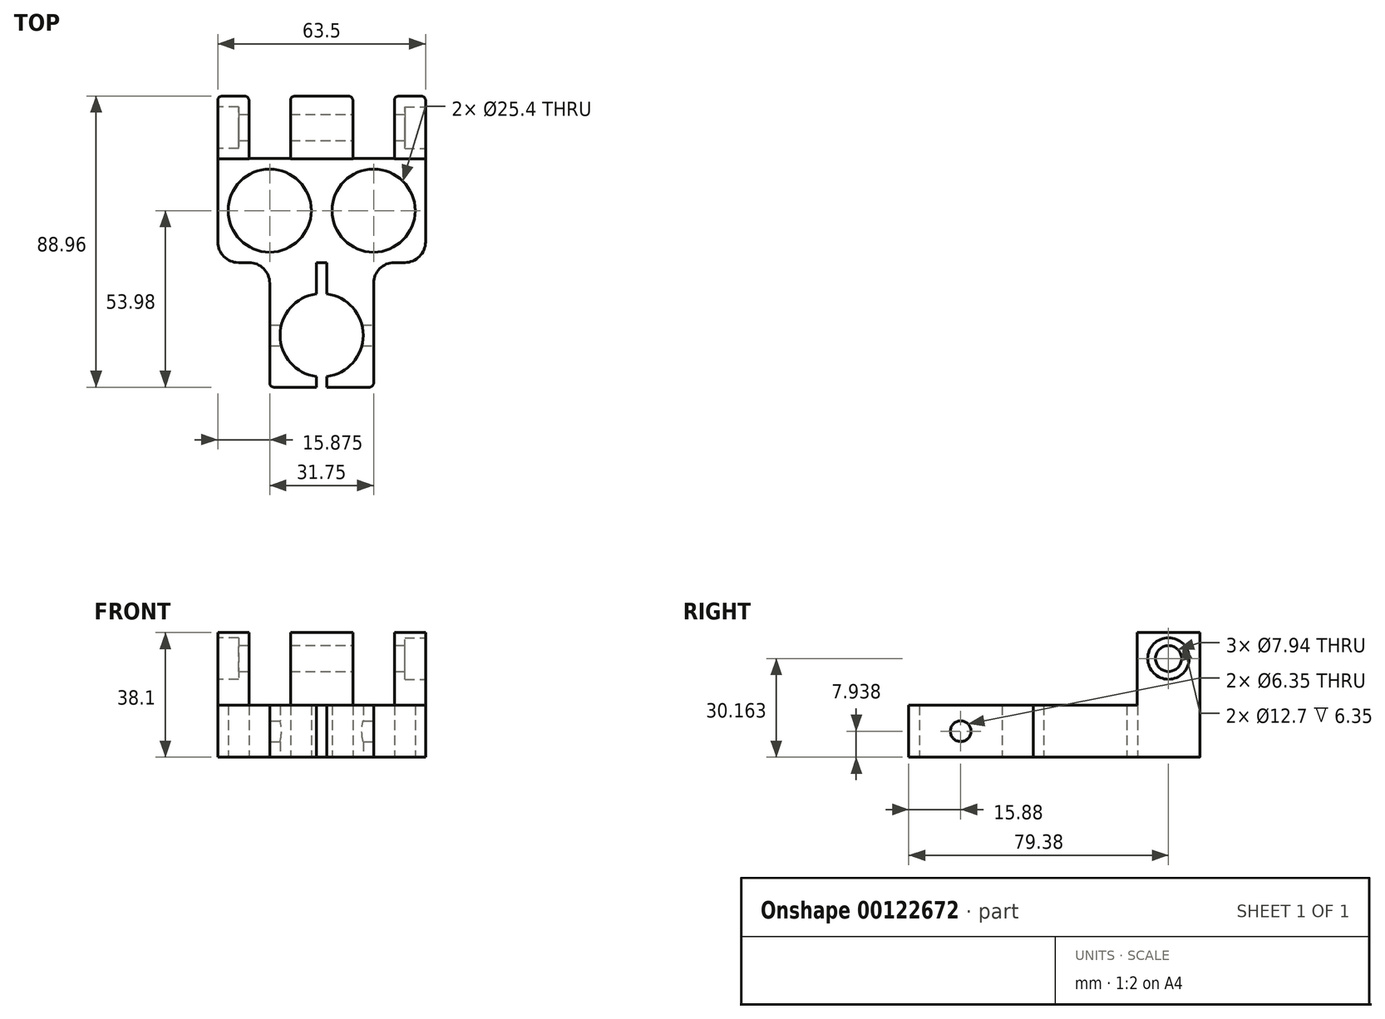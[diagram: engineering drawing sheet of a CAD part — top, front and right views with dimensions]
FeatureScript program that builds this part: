
annotation { "Feature Type Name" : "Feature", "Feature Type Description" : "" }
export const myFeature = defineFeature(function(context is Context, id is Id, definition is map)
    precondition{}
    {
        {
            var Q0;
            Q0=qCreatedBy(makeId("Top.planeOp"),FACE);
            var sketch = newSketch(context, id + "F0", { "sketchPlane" : qUnion([Q0])});
            skCircle(sketch, "E0", {"center": v(-15.88, 0) * mm, "radius": 12.7 * mm});
            skCircle(sketch, "E1", {"center": v(15.88, 0) * mm, "radius": 12.7 * mm});
            skArc(sketch, "E2", {"start": v(-1.59, -25.5) * mm, "mid": v(-12.7, -38.1) * mm, "end": v(-1.59, -50.7) * mm});
            skLineSegment(sketch, "E3", {"start": v(-14.6, -53.98) * mm, "end": v(-1.59, -53.98) * mm});
            skLineSegment(sketch, "E4", {"start": v(15.88, -52.7) * mm, "end": v(15.87, -22.23) * mm});
            skLineSegment(sketch, "E5", {"start": v(22.23, -15.88) * mm, "end": v(25.4, -15.88) * mm});
            skLineSegment(sketch, "E6", {"start": v(31.75, -9.53) * mm, "end": v(31.75, 33.7) * mm});
            skLineSegment(sketch, "E7", {"start": v(30.48, 34.98) * mm, "end": v(23.5, 34.98) * mm});
            skLineSegment(sketch, "E8", {"start": v(22.22, 33.7) * mm, "end": v(22.22, 15.99) * mm});
            skLineSegment(sketch, "E9", {"start": v(22.16, 15.93) * mm, "end": v(9.59, 15.93) * mm});
            skLineSegment(sketch, "E10", {"start": v(9.53, 15.99) * mm, "end": v(9.53, 33.7) * mm});
            skLineSegment(sketch, "E11", {"start": v(8.26, 34.98) * mm, "end": v(-8.26, 34.98) * mm});
            skLineSegment(sketch, "E12", {"start": v(-23.5, 34.98) * mm, "end": v(-30.48, 34.98) * mm});
            skLineSegment(sketch, "E13", {"start": v(-31.75, 33.7) * mm, "end": v(-31.75, -9.53) * mm});
            skLineSegment(sketch, "E14", {"start": v(-25.4, -15.88) * mm, "end": v(-22.23, -15.88) * mm});
            skLineSegment(sketch, "E15", {"start": v(-15.88, -22.23) * mm, "end": v(-15.88, -52.7) * mm});
            skPoint(sketch, "E16.visualSharp", {"position": v(-22.23, 15.93) * mm});
            skPoint(sketch, "E17.visualSharp", {"position": v(-9.53, 15.93) * mm});
            skPoint(sketch, "E18.visualSharp", {"position": v(9.53, 15.93) * mm});
            skArc(sketch, "E18.filletArc", {"start": v(9.53, 15.99) * mm, "mid": v(9.54, 15.94) * mm, "end": v(9.59, 15.93) * mm});
            skPoint(sketch, "E19.visualSharp", {"position": v(22.23, 15.93) * mm});
            skArc(sketch, "E19.filletArc", {"start": v(22.16, 15.93) * mm, "mid": v(22.2, 15.94) * mm, "end": v(22.22, 15.99) * mm});
            skPoint(sketch, "E20.visualSharp", {"position": v(-15.88, -15.88) * mm});
            skArc(sketch, "E20.filletArc", {"start": v(-15.87, -22.23) * mm, "mid": v(-17.73, -17.73) * mm, "end": v(-22.23, -15.87) * mm});
            skPoint(sketch, "E21.visualSharp", {"position": v(15.88, -15.88) * mm});
            skArc(sketch, "E21.filletArc", {"start": v(22.23, -15.87) * mm, "mid": v(17.73, -17.73) * mm, "end": v(15.87, -22.23) * mm});
            skPoint(sketch, "E22.visualSharp", {"position": v(-31.75, 34.98) * mm});
            skArc(sketch, "E22.filletArc", {"start": v(-30.48, 34.98) * mm, "mid": v(-31.38, 34.6) * mm, "end": v(-31.75, 33.7) * mm});
            skPoint(sketch, "E23.visualSharp", {"position": v(-22.22, 34.98) * mm});
            skArc(sketch, "E23.filletArc", {"start": v(-22.22, 33.7) * mm, "mid": v(-22.6, 34.6) * mm, "end": v(-23.5, 34.98) * mm});
            skPoint(sketch, "E24.visualSharp", {"position": v(-9.53, 34.98) * mm});
            skArc(sketch, "E24.filletArc", {"start": v(-8.26, 34.98) * mm, "mid": v(-9.15, 34.6) * mm, "end": v(-9.53, 33.7) * mm});
            skPoint(sketch, "E25.visualSharp", {"position": v(9.53, 34.98) * mm});
            skArc(sketch, "E25.filletArc", {"start": v(9.53, 33.7) * mm, "mid": v(9.15, 34.6) * mm, "end": v(8.26, 34.98) * mm});
            skPoint(sketch, "E26.visualSharp", {"position": v(22.22, 34.98) * mm});
            skArc(sketch, "E26.filletArc", {"start": v(23.5, 34.98) * mm, "mid": v(22.6, 34.6) * mm, "end": v(22.22, 33.7) * mm});
            skPoint(sketch, "E27.visualSharp", {"position": v(31.75, 34.98) * mm});
            skArc(sketch, "E27.filletArc", {"start": v(31.75, 33.7) * mm, "mid": v(31.38, 34.6) * mm, "end": v(30.48, 34.98) * mm});
            skPoint(sketch, "E28.visualSharp", {"position": v(31.75, -15.88) * mm});
            skPoint(sketch, "E29.visualSharp", {"position": v(-31.75, -15.88) * mm});
            skPoint(sketch, "E30.visualSharp", {"position": v(-15.88, -53.98) * mm});
            skArc(sketch, "E30.filletArc", {"start": v(-15.88, -52.7) * mm, "mid": v(-15.5, -53.6) * mm, "end": v(-14.6, -53.98) * mm});
            skPoint(sketch, "E31.visualSharp", {"position": v(15.88, -53.98) * mm});
            skArc(sketch, "E31.filletArc", {"start": v(14.6, -53.98) * mm, "mid": v(15.5, -53.6) * mm, "end": v(15.88, -52.7) * mm});
            skLineSegment(sketch, "E32", {"start": v(-1.59, -15.88) * mm, "end": v(1.59, -15.88) * mm});
            skLineSegment(sketch, "E33.trimOffspring", {"start": v(1.59, -53.98) * mm, "end": v(14.6, -53.98) * mm});
            skLineSegment(sketch, "E34", {"start": v(-22.22, 33.7) * mm, "end": v(-22.23, 15.93) * mm});
            skLineSegment(sketch, "E35", {"start": v(-9.53, 15.93) * mm, "end": v(-9.53, 33.7) * mm});
            skLineSegment(sketch, "E36", {"start": v(-22.23, 15.93) * mm, "end": v(-9.53, 15.93) * mm});
            skArc(sketch, "E37.filletArc", {"start": v(-31.75, -9.53) * mm, "mid": v(-29.9, -14.02) * mm, "end": v(-25.4, -15.88) * mm});
            skArc(sketch, "E38.filletArc", {"start": v(25.4, -15.88) * mm, "mid": v(29.9, -14.02) * mm, "end": v(31.75, -9.53) * mm});
            skLineSegment(sketch, "E39.trimOffspring", {"start": v(-1.59, -25.5) * mm, "end": v(-1.59, -15.88) * mm});
            skLineSegment(sketch, "E40", {"start": v(1.59, -53.98) * mm, "end": v(1.59, -50.7) * mm});
            skLineSegment(sketch, "E41", {"start": v(-1.59, -53.98) * mm, "end": v(-1.59, -50.7) * mm});
            skLineSegment(sketch, "E42", {"start": v(1.59, -15.88) * mm, "end": v(1.59, -25.5) * mm});
            skArc(sketch, "E43.trimOffspring", {"start": v(1.59, -50.7) * mm, "mid": v(12.7, -38.1) * mm, "end": v(1.59, -25.5) * mm});
            skSolve(sketch);
        }
        {
            var Q0;
            Q0=makeQuery(id+"F0.imprint","IMPRINT",FACE,{"disambiguationData":[TD([[makeQuery(id+"F0.imprint","IMPRINT",EDGE,{"derivedFrom":sQuery(id+"F0.wireOp",EDGE,"E0")}),-1.0]])]});
            extrude(context, id + "F1", {"entities" : qUnion([Q0]), "depth" : 38.1 * mm});
        }
        {
            var Q0;
            Q0=makeQuery(id+"F1.opExtrude","SWEPT_FACE",FACE,{"disambiguationData":[OSD([sQuery(id+"F0.wireOp",EDGE,"E6")])]});
            var sketch = newSketch(context, id + "F2", { "sketchPlane" : qUnion([Q0])});
            skLineSegment(sketch, "E44.bottom", {"start": v(-53.97, 15.88) * mm, "end": v(15.88, 15.88) * mm});
            skLineSegment(sketch, "E44.top", {"start": v(-53.97, 38.1) * mm, "end": v(15.88, 38.1) * mm});
            skLineSegment(sketch, "E44.left", {"start": v(-53.97, 15.88) * mm, "end": v(-53.97, 38.1) * mm});
            skLineSegment(sketch, "E45", {"start": v(15.88, 38.1) * mm, "end": v(15.88, 15.88) * mm});
            skSolve(sketch);
        }
        {
            var Q0;
            Q0=qSketchRegion(id+"F2",true);
            extrude(context, id + "F3", {"entities" : qUnion([Q0]), "operationType" : NewBodyOperationType.REMOVE, "endBound" : BoundingType.THROUGH_ALL, "oppositeDirection" : true, "depth" : 25.4 * mm});
        }
        {
            var Q0;
            Q0=makeQuery(id+"F1.opExtrude","SWEPT_FACE",FACE,{"disambiguationData":[OSD([sQuery(id+"F0.wireOp",EDGE,"E7")])]});
            var sketch = newSketch(context, id + "F4", { "sketchPlane" : qUnion([Q0])});
            skLineSegment(sketch, "E46.bottom", {"start": v(-22.22, 45.37) * mm, "end": v(-9.53, 45.37) * mm});
            skLineSegment(sketch, "E46.top", {"start": v(-22.22, 15.88) * mm, "end": v(-9.52, 15.88) * mm});
            skLineSegment(sketch, "E46.left", {"start": v(-22.22, 45.37) * mm, "end": v(-22.22, 15.88) * mm});
            skLineSegment(sketch, "E46.right", {"start": v(-9.53, 45.37) * mm, "end": v(-9.53, 15.88) * mm});
            skLineSegment(sketch, "E47.bottom", {"start": v(9.53, 45.37) * mm, "end": v(22.22, 45.37) * mm});
            skLineSegment(sketch, "E47.top", {"start": v(9.52, 15.88) * mm, "end": v(22.22, 15.88) * mm});
            skLineSegment(sketch, "E47.left", {"start": v(9.52, 45.37) * mm, "end": v(9.53, 15.88) * mm});
            skLineSegment(sketch, "E47.right", {"start": v(22.22, 45.37) * mm, "end": v(22.22, 15.88) * mm});
            skSolve(sketch);
        }
        {
            var Q0;
            Q0=makeQuery(id+"F4.imprint","IMPRINT",FACE,{"disambiguationData":[TD([[makeQuery(id+"F4.imprint","IMPRINT",EDGE,{"derivedFrom":sQuery(id+"F4.wireOp",EDGE,"E47.bottom")}),-1.0]])]});
            var Q1;
            Q1=makeQuery(id+"F4.imprint","IMPRINT",FACE,{"disambiguationData":[TD([[makeQuery(id+"F4.imprint","IMPRINT",EDGE,{"derivedFrom":sQuery(id+"F4.wireOp",EDGE,"E46.bottom")}),-1.0]])]});
            extrude(context, id + "F5", {"entities" : qUnion([Q0, Q1]), "operationType" : NewBodyOperationType.REMOVE, "endBound" : BoundingType.THROUGH_ALL, "oppositeDirection" : true, "depth" : 25.4 * mm});
        }
        {
            var Q0;
            Q0=makeQuery(id+"F1.opExtrude","SWEPT_FACE",FACE,{"disambiguationData":[OSD([sQuery(id+"F0.wireOp",EDGE,"E6")])]});
            var sketch = newSketch(context, id + "F6", { "sketchPlane" : qUnion([Q0])});
            skCircle(sketch, "E48", {"center": v(-38.1, 7.94) * mm, "radius": 3.17 * mm});
            skCircle(sketch, "E49", {"center": v(25.4, 30.16) * mm, "radius": 3.97 * mm});
            skSolve(sketch);
        }
        {
            var Q0;
            Q0=makeQuery(id+"F6.imprint","IMPRINT",FACE,{"disambiguationData":[TD([[makeQuery(id+"F6.imprint","IMPRINT",EDGE,{"derivedFrom":sQuery(id+"F6.wireOp",EDGE,"E49")}),1.0]])]});
            var Q1;
            Q1=makeQuery(id+"F6.imprint","IMPRINT",FACE,{"disambiguationData":[TD([[makeQuery(id+"F6.imprint","IMPRINT",EDGE,{"derivedFrom":sQuery(id+"F6.wireOp",EDGE,"E48")}),1.0]])]});
            extrude(context, id + "F7", {"entities" : qUnion([Q0, Q1]), "operationType" : NewBodyOperationType.REMOVE, "endBound" : BoundingType.THROUGH_ALL, "oppositeDirection" : true, "depth" : 25.4 * mm});
        }
        {
            var Q0;
            Q0=makeQuery(id+"F1.opExtrude","SWEPT_FACE",FACE,{"disambiguationData":[OSD([sQuery(id+"F0.wireOp",EDGE,"E6")])]});
            var sketch = newSketch(context, id + "F8", { "sketchPlane" : qUnion([Q0])});
            skCircle(sketch, "E50", {"center": v(25.4, 30.16) * mm, "radius": 6.35 * mm});
            skSolve(sketch);
        }
        {
            var Q0;
            Q0=qSketchRegion(id+"F8",true);
            extrude(context, id + "F9", {"entities" : qUnion([Q0]), "operationType" : NewBodyOperationType.REMOVE, "oppositeDirection" : true, "depth" : 6.35 * mm});
        }
        {
            var Q0;
            Q0=makeQuery(id+"F1.opExtrude","SWEPT_FACE",FACE,{"disambiguationData":[OSD([sQuery(id+"F0.wireOp",EDGE,"E13")])]});
            var sketch = newSketch(context, id + "F10", { "sketchPlane" : qUnion([Q0])});
            skCircle(sketch, "E51", {"center": v(-25.4, 30.16) * mm, "radius": 6.35 * mm});
            skSolve(sketch);
        }
        {
            var Q0;
            Q0=makeQuery(id+"F10.imprint","IMPRINT",FACE,{"disambiguationData":[TD([[makeQuery(id+"F10.imprint","IMPRINT",EDGE,{"derivedFrom":sQuery(id+"F10.wireOp",EDGE,"E51")}),1.0]])]});
            extrude(context, id + "F11", {"entities" : qUnion([Q0]), "operationType" : NewBodyOperationType.REMOVE, "oppositeDirection" : true, "depth" : 6.35 * mm});
        }
    });
